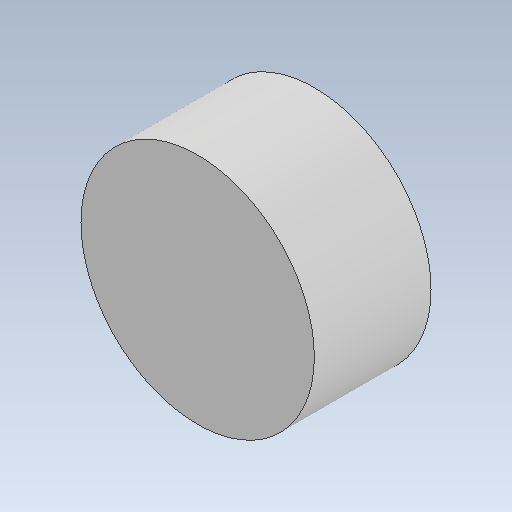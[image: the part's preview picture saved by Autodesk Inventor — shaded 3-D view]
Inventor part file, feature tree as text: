
AUTODESK INVENTOR PART (.ipt)
format: ipt  version: 2021 (Build 250183000, 183)  size: 91,136 bytes
history: native  units: mm
features: extrude x1, sketch x1
ambient origin geometry x8: Origin, YZ Plane, XZ Plane, XY Plane, X Axis, Y Axis, Z Axis, Center Point
bodies: Solid1 (feature_tree)
feature tree (2):
  extrude  "Extrusion1"  Depth=10.0mm
  sketch  "Sketch1"  dims[d0=10.0mm d1=0.0mm d2=20.0mm]
